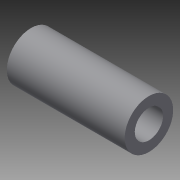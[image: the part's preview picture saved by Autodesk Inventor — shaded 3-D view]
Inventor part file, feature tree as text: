
AUTODESK INVENTOR PART (.ipt)
format: ipt  version: 2015 (Build 190159000, 159)  size: 77,312 bytes
history: native  units: in
note: dims shown in document units (in); Inventor stores cm internally (conversion verified against a paired STEP export)
features: extrude x1, sketch x1
ambient origin geometry x8: Origin, YZ Plane, XZ Plane, XY Plane, X Axis, Y Axis, Z Axis, Center Point
bodies: Solid1 (feature_tree)
feature tree (2):
  extrude  "Extrusion1"  Depth=0.695in
  sketch  "Sketch1"  dims[d0=0.695in d1=0.0in d2=0.167in]
